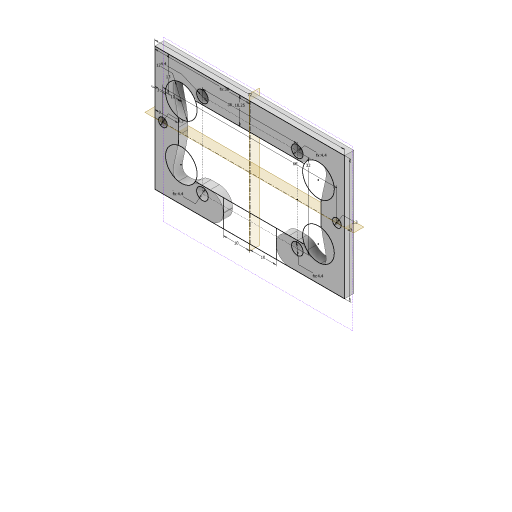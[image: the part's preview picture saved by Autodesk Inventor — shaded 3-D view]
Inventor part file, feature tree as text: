
AUTODESK INVENTOR PART (.ipt)
format: ipt  version: 2023 (Build 270158000, 158)  size: 238,592 bytes
history: native  units: mm
features: extrude x4, sketch x2, fillet x2, plane x2, mirror x2, other x1
ambient origin geometry x8: Origin, YZ Plane, XZ Plane, XY Plane, X Axis, Y Axis, Z Axis, Center Point
bodies: Solid1 (feature_tree)
feature tree (13):
  sketch  "Sketch1"  dims[d0=72.0mm d1=47.0mm]
  extrude  "Extrusion1"  Depth=47.0mm
  extrude  "Extrusion2"  Depth=3.3mm
  fillet  "Fillet1"  Radius=66.0mm
  extrude  "Extrusion3"  Depth=3.0mm
  fillet  "Fillet2"  Radius=36.0mm
  extrude  "Extrusion4"  Depth=32.0mm
  plane  "Work Plane1"
  mirror  "Mirror1"
  plane  "Work Plane2"
  mirror  "Mirror2"
  other  "Image2"
  sketch  "Sketch2"  dims[d2=3.3mm d3=3.3mm d4=66.0mm d5=3.0mm d6=36.0mm d7=32.0mm d8=36.0mm d9=4.4mm d10=4.4mm d11=4.4mm d12=4.4mm d32=12.0mm d33=10.0mm d34=13.0mm d35=9.0mm d36=10.25mm d39=3.5mm d40=0.0mm d41=0.0mm d42=-1.22173mm d43=5.0mm d44=10.0mm d45=10.0mm d46=2.0mm d47=0.0mm d48=5.0mm d50=1.0mm d51=10.0mm d52=0.0mm]
